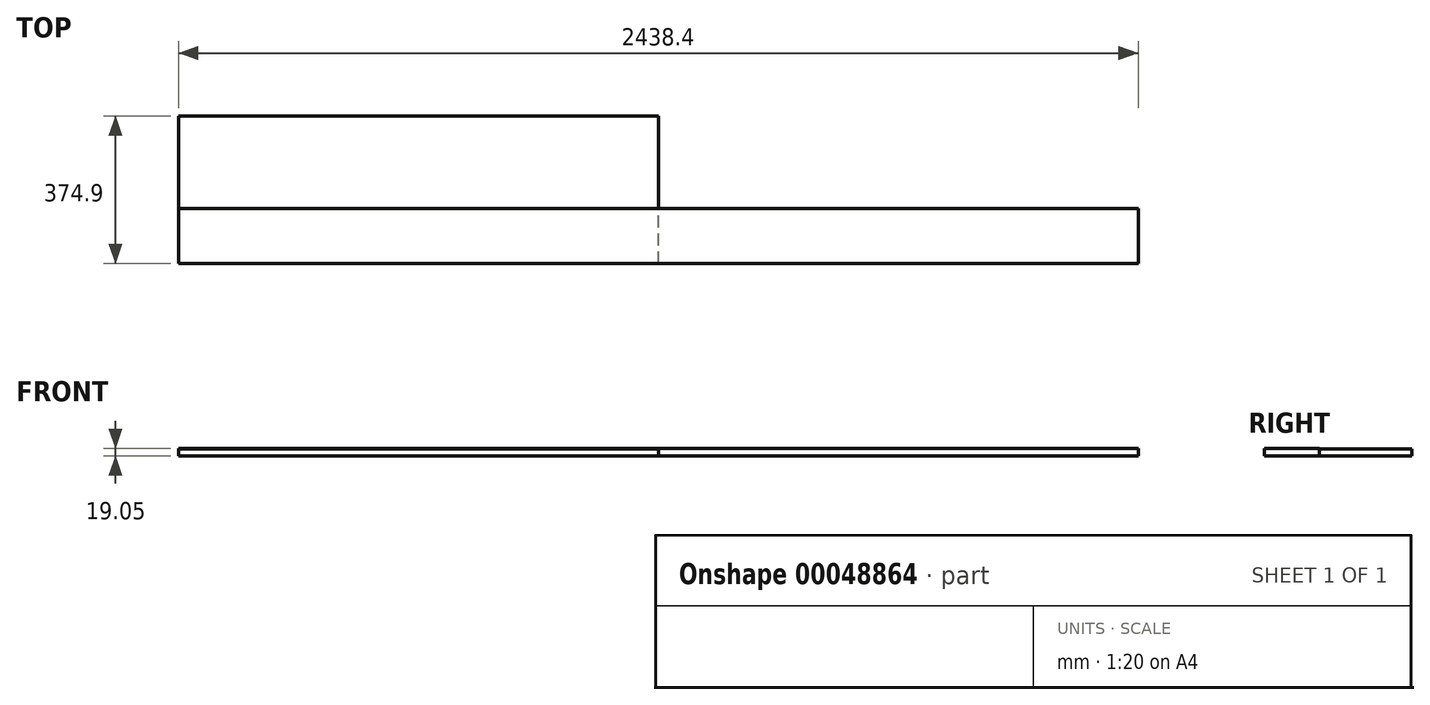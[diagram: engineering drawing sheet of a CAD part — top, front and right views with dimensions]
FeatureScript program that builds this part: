
annotation { "Feature Type Name" : "Feature", "Feature Type Description" : "" }
export const myFeature = defineFeature(function(context is Context, id is Id, definition is map)
    precondition{}
    {
        {
            var Q0;
            Q0=qCreatedBy(makeId("Top.planeOp"),FACE);
            var sketch = newSketch(context, id + "F0", { "sketchPlane" : qUnion([Q0])});
            skLineSegment(sketch, "E0.bottom", {"start": v(0, 0) * mm, "end": v(1219.2, 0) * mm});
            skLineSegment(sketch, "E0.top", {"start": v(0, 374.9) * mm, "end": v(1219.2, 374.9) * mm});
            skLineSegment(sketch, "E0.left", {"start": v(0, 0) * mm, "end": v(0, 374.9) * mm});
            skLineSegment(sketch, "E0.right", {"start": v(1219.2, 0) * mm, "end": v(1219.2, 374.9) * mm});
            skSolve(sketch);
        }
        {
            var Q0;
            Q0 = qSketchRegion(id + "F0", true);
            extrude(context, id + "F1", {"entities" : qUnion([Q0]), "depth" : 18 * mm});
        }
        {
            var Q0;
            Q0=qCreatedBy(makeId("Top.planeOp"),FACE);
            var sketch = newSketch(context, id + "F2", { "sketchPlane" : qUnion([Q0])});
            skLineSegment(sketch, "E1.bottom", {"start": v(0, 0) * mm, "end": v(2438.4, 0) * mm});
            skLineSegment(sketch, "E1.top", {"start": v(0, 139.7) * mm, "end": v(2438.4, 139.7) * mm});
            skLineSegment(sketch, "E1.left", {"start": v(0, 0) * mm, "end": v(0, 139.7) * mm});
            skLineSegment(sketch, "E1.right", {"start": v(2438.4, 0) * mm, "end": v(2438.4, 139.7) * mm});
            skSolve(sketch);
        }
        {
            var Q0;
            Q0=makeQuery(id+"F2.imprint","IMPRINT",FACE,{"disambiguationData":[TD([[makeQuery(id+"F2.imprint","IMPRINT",EDGE,{"derivedFrom":sQuery(id+"F2.wireOp",EDGE,"E1.bottom")}),1.0]])]});
            extrude(context, id + "F3", {"entities" : qUnion([Q0]), "depth" : 19.05 * mm});
        }
    });
